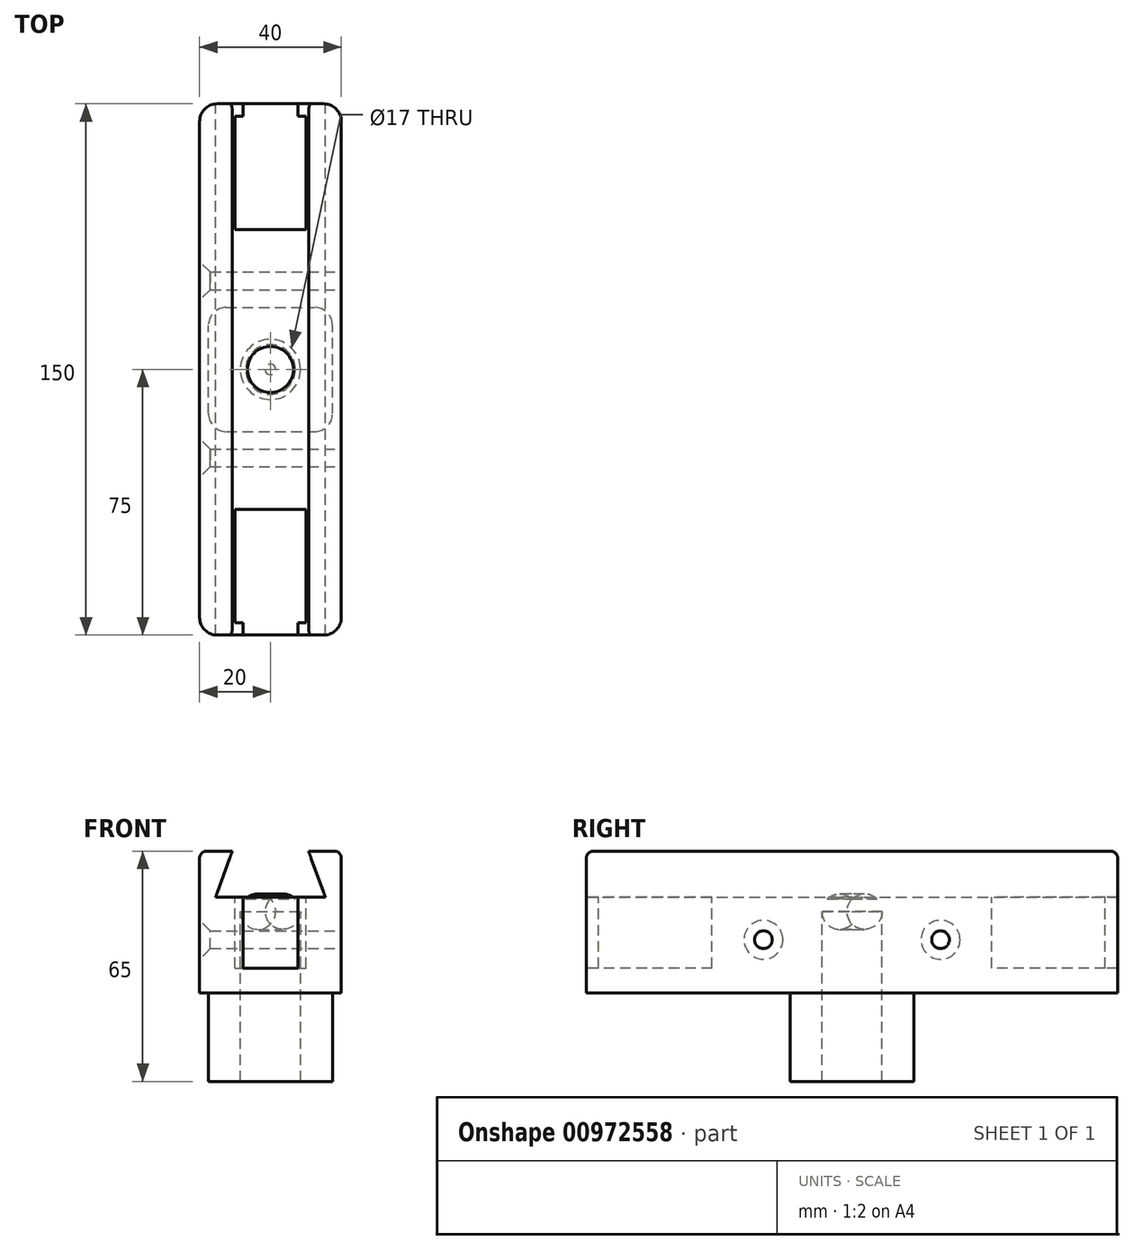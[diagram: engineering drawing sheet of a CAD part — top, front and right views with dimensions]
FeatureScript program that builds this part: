
annotation { "Feature Type Name" : "Feature", "Feature Type Description" : "" }
export const myFeature = defineFeature(function(context is Context, id is Id, definition is map)
    precondition{}
    {
        {
            var Q0;
            Q0=qCreatedBy(makeId("Front.planeOp"),FACE);
            var sketch = newSketch(context, id + "F0", { "sketchPlane" : qUnion([Q0])});
            skLineSegment(sketch, "E0.bottom", {"start": v(-20, 13.5) * mm, "end": v(20, 13.5) * mm});
            skLineSegment(sketch, "E0.top", {"start": v(-20, -13.5) * mm, "end": v(20, -13.5) * mm});
            skLineSegment(sketch, "E0.left", {"start": v(-20, 13.5) * mm, "end": v(-20, -13.5) * mm});
            skLineSegment(sketch, "E0.right", {"start": v(20, 13.5) * mm, "end": v(20, -13.5) * mm});
            skPoint(sketch, "E0.middle", {"position": v(0, 0) * mm});
            skSolve(sketch);
        }
        {
            var Q0;
            Q0=makeQuery(id+"F0.imprint","IMPRINT",FACE,{"disambiguationData":[TD([[makeQuery(id+"F0.imprint","IMPRINT",EDGE,{"derivedFrom":sQuery(id+"F0.wireOp",EDGE,"E0.bottom")}),-1.0]])]});
            extrude(context, id + "F1", {"entities" : qUnion([Q0]), "depth" : 150 * mm, "offsetDistance" : 25 * mm});
        }
        {
            var Q0;
            Q0=makeQuery(id+"F1.opExtrude","SWEPT_FACE",FACE,{"disambiguationData":[OSD([sQuery(id+"F0.wireOp",EDGE,"E0.bottom")])]});
            var sketch = newSketch(context, id + "F2", { "sketchPlane" : qUnion([Q0])});
            skLineSegment(sketch, "E1", {"start": v(1.02, -154.13) * mm, "end": v(0, 16.76) * mm, "construction": true});
            skLineSegment(sketch, "E2", {"start": v(-20, -75) * mm, "end": v(29.97, -74.7) * mm, "construction": true});
            skLineSegment(sketch, "E3", {"start": v(-20, -75) * mm, "end": v(-25.89, -75.04) * mm, "construction": true});
            skCircle(sketch, "E4", {"center": v(0.55, -74.88) * mm, "radius": 7.75 * mm});
            skLineSegment(sketch, "E5.bottom", {"start": v(-10, -3.5) * mm, "end": v(10, -3.5) * mm});
            skLineSegment(sketch, "E5.top", {"start": v(-10, -35.5) * mm, "end": v(10, -35.5) * mm});
            skLineSegment(sketch, "E5.left", {"start": v(-10, -3.5) * mm, "end": v(-10, -35.5) * mm});
            skLineSegment(sketch, "E5.right", {"start": v(10, -3.5) * mm, "end": v(10, -35.5) * mm});
            skLineSegment(sketch, "E6.bottom", {"start": v(-10, -114.5) * mm, "end": v(10, -114.5) * mm});
            skLineSegment(sketch, "E6.top", {"start": v(-10, -146.5) * mm, "end": v(10, -146.5) * mm});
            skLineSegment(sketch, "E6.left", {"start": v(-10, -114.5) * mm, "end": v(-10, -146.5) * mm});
            skLineSegment(sketch, "E6.right", {"start": v(10, -114.5) * mm, "end": v(10, -146.5) * mm});
            skLineSegment(sketch, "E7.bottom", {"start": v(-7.75, 0) * mm, "end": v(7.75, 0) * mm});
            skLineSegment(sketch, "E7.top", {"start": v(-7.75, -3.5) * mm, "end": v(7.75, -3.5) * mm});
            skLineSegment(sketch, "E7.left", {"start": v(-7.75, 0) * mm, "end": v(-7.75, -3.5) * mm});
            skLineSegment(sketch, "E7.right", {"start": v(7.75, 0) * mm, "end": v(7.75, -3.5) * mm});
            skLineSegment(sketch, "E8.bottom", {"start": v(-7.75, -146.5) * mm, "end": v(7.75, -146.5) * mm});
            skLineSegment(sketch, "E8.top", {"start": v(-7.75, -150) * mm, "end": v(7.75, -150) * mm});
            skLineSegment(sketch, "E8.left", {"start": v(-7.75, -146.5) * mm, "end": v(-7.75, -150) * mm});
            skLineSegment(sketch, "E8.right", {"start": v(7.75, -146.5) * mm, "end": v(7.75, -150) * mm});
            skSolve(sketch);
        }
        {
            var Q0;
            Q0=makeQuery(id+"F2.imprint","IMPRINT",FACE,{"disambiguationData":[TD([[makeQuery(id+"F2.imprint","IMPRINT",EDGE,{"derivedFrom":sQuery(id+"F2.wireOp",EDGE,"E7.bottom")}),-1.0]])]});
            var Q1;
            Q1=makeQuery(id+"F2.imprint","IMPRINT",FACE,{"disambiguationData":[TD([[makeQuery(id+"F2.imprint","IMPRINT",EDGE,{"derivedFrom":sQuery(id+"F2.wireOp",EDGE,"E5.top")}),1.0]])]});
            var Q2;
            Q2=makeQuery(id+"F2.imprint","IMPRINT",FACE,{"disambiguationData":[TD([[makeQuery(id+"F2.imprint","IMPRINT",EDGE,{"derivedFrom":sQuery(id+"F2.wireOp",EDGE,"E6.bottom")}),-1.0]])]});
            var Q3;
            Q3=makeQuery(id+"F2.imprint","IMPRINT",FACE,{"disambiguationData":[TD([[makeQuery(id+"F2.imprint","IMPRINT",EDGE,{"derivedFrom":sQuery(id+"F2.wireOp",EDGE,"E8.top")}),1.0]])]});
            extrude(context, id + "F3", {"entities" : qUnion([Q0, Q1, Q2, Q3]), "operationType" : NewBodyOperationType.REMOVE, "oppositeDirection" : true, "depth" : 20 * mm, "offsetDistance" : 25 * mm});
        }
        {
            var Q0;
            Q0=makeQuery(id+"F1.opExtrude","SWEPT_FACE",FACE,{"disambiguationData":[OSD([sQuery(id+"F0.wireOp",EDGE,"E0.top")])]});
            var sketch = newSketch(context, id + "F4", { "sketchPlane" : qUnion([Q0])});
            skLineSegment(sketch, "E9", {"start": v(0, 153.56) * mm, "end": v(0, -4.66) * mm, "construction": true});
            skLineSegment(sketch, "E10", {"start": v(-27.94, 75) * mm, "end": v(35.68, 75) * mm, "construction": true});
            skPoint(sketch, "E10.startSnap0", {"position": v(-20, 75) * mm});
            skCircle(sketch, "E11", {"center": v(0, 75) * mm, "radius": 8.5 * mm});
            skSolve(sketch);
        }
        {
            var Q0;
            Q0=makeQuery(id+"F4.imprint","IMPRINT",FACE,{"disambiguationData":[TD([[makeQuery(id+"F4.imprint","IMPRINT",EDGE,{"derivedFrom":sQuery(id+"F4.wireOp",EDGE,"E11")}),-1.0]])]});
            var sketch = newSketch(context, id + "F5", { "sketchPlane" : qUnion([Q0])});
            skLineSegment(sketch, "E12.bottom", {"start": v(-17.5, 92.5) * mm, "end": v(17.5, 92.5) * mm});
            skLineSegment(sketch, "E12.top", {"start": v(-17.5, 57.5) * mm, "end": v(17.5, 57.5) * mm});
            skLineSegment(sketch, "E12.left", {"start": v(-17.5, 92.5) * mm, "end": v(-17.5, 57.5) * mm});
            skLineSegment(sketch, "E12.right", {"start": v(17.5, 92.5) * mm, "end": v(17.5, 57.5) * mm});
            skPoint(sketch, "E12.middle", {"position": v(0, 75) * mm});
            skSolve(sketch);
        }
        {
            var Q0;
            Q0=makeQuery(id+"F5.imprint","IMPRINT",FACE,{"disambiguationData":[TD([[makeQuery(id+"F5.imprint","IMPRINT",EDGE,{"derivedFrom":sQuery(id+"F5.wireOp",EDGE,"E12.bottom")}),-1.0]])]});
            extrude(context, id + "F6", {"entities" : qUnion([Q0]), "operationType" : NewBodyOperationType.ADD, "depth" : 25 * mm, "offsetDistance" : 25 * mm});
        }
        {
            var Q0;
            Q0=makeQuery(id+"F4.imprint","IMPRINT",FACE,{"disambiguationData":[TD([[makeQuery(id+"F4.imprint","IMPRINT",EDGE,{"derivedFrom":sQuery(id+"F4.wireOp",EDGE,"E11")}),1.0]])]});
            extrude(context, id + "F7", {"entities" : qUnion([Q0]), "operationType" : NewBodyOperationType.REMOVE, "oppositeDirection" : true, "depth" : 25 * mm, "offsetDistance" : 25 * mm});
        }
        {
            var Q0;
            Q0=makeQuery(id+"F1.opExtrude","SWEPT_FACE",FACE,{"disambiguationData":[OSD([sQuery(id+"F0.wireOp",EDGE,"E0.bottom")])]});
            var sketch = newSketch(context, id + "F8", { "sketchPlane" : qUnion([Q0])});
            skLineSegment(sketch, "E13", {"start": v(0, 0) * mm, "end": v(0, -150.24) * mm, "construction": true});
            skLineSegment(sketch, "E14", {"start": v(-20, -75) * mm, "end": v(33, -75) * mm, "construction": true});
            skCircle(sketch, "E15", {"center": v(0, -75) * mm, "radius": 5.5 * mm});
            skSolve(sketch);
        }
        {
            var Q0;
            Q0=makeQuery(id+"F8.imprint","IMPRINT",FACE,{"disambiguationData":[TD([[makeQuery(id+"F8.imprint","IMPRINT",EDGE,{"derivedFrom":sQuery(id+"F8.wireOp",EDGE,"E15")}),1.0]])]});
            extrude(context, id + "F9", {"entities" : qUnion([Q0]), "operationType" : NewBodyOperationType.REMOVE, "endBound" : BoundingType.THROUGH_ALL, "oppositeDirection" : true, "depth" : 2 * mm, "offsetDistance" : 25 * mm});
        }
        {
            var Q0;
            Q0=makeQuery(id+"F9.boolean.opBoolean","INTERSECT",EDGE,{"derivedFrom":[makeQuery(id+"F7.boolean.opBoolean","COPY",FACE,{"derivedFrom":makeQuery(id+"F7.opExtrude","CAP_FACE",FACE,{"disambiguationData":[OSD([sQuery(id+"F4.wireOp",EDGE,"E11")])],"isStart":false})}),makeQuery(id+"F9.opExtrude","SWEPT_FACE",FACE,{"disambiguationData":[OSD([sQuery(id+"F8.wireOp",EDGE,"E15")])]})]});
            chamfer(context, id + "F10", {"entities" : qUnion([Q0]), "width" : 3 * mm, "tangentPropagation" : true});
        }
        {
            var Q0;
            {var subQ0=sQuery(id+"F4.wireOp",EDGE,"E11");Q0=makeQuery(id+"F10.opChamfer","BLEND_EDGE",EDGE,{"blendedFrom":[makeQuery(id+"F9.boolean.opBoolean","INTERSECT",EDGE,{"derivedFrom":[makeQuery(id+"F7.boolean.opBoolean","COPY",FACE,{"derivedFrom":makeQuery(id+"F7.opExtrude","CAP_FACE",FACE,{"disambiguationData":[OSD([subQ0])],"isStart":false})}),makeQuery(id+"F9.opExtrude","SWEPT_FACE",FACE,{"disambiguationData":[OSD([sQuery(id+"F8.wireOp",EDGE,"E15")])]})]}),makeQuery(id+"F7.boolean.opBoolean","MERGE",FACE,{"derivedFrom":[makeQuery(id+"F6.opExtrude","SWEPT_FACE",FACE,{"disambiguationData":[OSD([subQ0])]})],"fromTools":[makeQuery(id+"F7.opExtrude","SWEPT_FACE",FACE,{"disambiguationData":[OSD([subQ0])]})]})],"blendedInto":[makeQuery(id+"F7.boolean.opBoolean","MERGE",FACE,{"derivedFrom":[makeQuery(id+"F6.opExtrude","SWEPT_FACE",FACE,{"disambiguationData":[OSD([subQ0])]})],"fromTools":[makeQuery(id+"F7.opExtrude","SWEPT_FACE",FACE,{"disambiguationData":[OSD([subQ0])]})]})]});}
            fillet(context, id + "F11", {"entities" : qUnion([Q0]), "radius" : 5 * mm, "tangentPropagation" : true, "allowEdgeOverflow" : false});
        }
        {
            var Q0;
            Q0=qCreatedBy(makeId("Front.planeOp"),FACE);
            var sketch = newSketch(context, id + "F12", { "sketchPlane" : qUnion([Q0])});
            skLineSegment(sketch, "E16.bottom", {"start": v(-20, 13.5) * mm, "end": v(20, 13.5) * mm});
            skLineSegment(sketch, "E16.top", {"start": v(-20, 26.5) * mm, "end": v(20, 26.5) * mm});
            skLineSegment(sketch, "E16.left", {"start": v(-20, 13.5) * mm, "end": v(-20, 26.5) * mm});
            skLineSegment(sketch, "E16.right", {"start": v(20, 13.5) * mm, "end": v(20, 26.5) * mm});
            skLineSegment(sketch, "E17", {"start": v(-15.5, 13.5) * mm, "end": v(15.5, 13.5) * mm});
            skLineSegment(sketch, "E18", {"start": v(15.5, 13.5) * mm, "end": v(10.77, 26.5) * mm});
            skLineSegment(sketch, "E19", {"start": v(10.77, 26.5) * mm, "end": v(-10.77, 26.5) * mm});
            skLineSegment(sketch, "E20", {"start": v(-10.77, 26.5) * mm, "end": v(-15.5, 13.5) * mm});
            skLineSegment(sketch, "E21", {"start": v(-15.5, 13.5) * mm, "end": v(-15.5, 27.62) * mm, "construction": true});
            skLineSegment(sketch, "E22", {"start": v(15.5, 13.5) * mm, "end": v(15.5, 28) * mm, "construction": true});
            skSolve(sketch);
        }
        {
            var Q0;
            {var subQ0=sQuery(id+"F12.wireOp",EDGE,"E16.right");Q0=makeQuery(id+"F12.imprint","IMPRINT",FACE,{"disambiguationData":[TD([[makeQuery(id+"F12.imprint","IMPRINT",EDGE,{"derivedFrom":subQ0}),1.0]])]});}
            var Q1;
            {var subQ0=sQuery(id+"F12.wireOp",EDGE,"E16.left");Q1=makeQuery(id+"F12.imprint","IMPRINT",FACE,{"disambiguationData":[TD([[makeQuery(id+"F12.imprint","IMPRINT",EDGE,{"derivedFrom":subQ0}),-1.0]])]});}
            var Q2;
            Q2=makeQuery(id+"F1.opExtrude","CAP_FACE",FACE,{"disambiguationData":[OSD([sQuery(id+"F0.wireOp",EDGE,"E0.bottom"),sQuery(id+"F0.wireOp",EDGE,"E0.top"),sQuery(id+"F0.wireOp",EDGE,"E0.left"),sQuery(id+"F0.wireOp",EDGE,"E0.right")])],"isStart":false});
            extrude(context, id + "F13", {"entities" : qUnion([Q0, Q1]), "operationType" : NewBodyOperationType.ADD, "endBound" : BoundingType.UP_TO_SURFACE, "depth" : 25 * mm, "endBoundEntityFace" : qUnion([Q2]), "offsetDistance" : 25 * mm});
        }
        {
            var Q0;
            Q0=makeQuery(id+"F13.boolean.opBoolean","MERGE",EDGE,{"derivedFrom":[makeQuery(id+"F1.opExtrude","CAP_EDGE",EDGE,{"disambiguationData":[OSD([sQuery(id+"F0.wireOp",EDGE,"E0.left")])],"isStart":false}),makeQuery(id+"F13.opExtrude","CAP_EDGE",EDGE,{"disambiguationData":[OSD([sQuery(id+"F12.wireOp",EDGE,"E16.left")])],"isStart":false})]});
            var Q1;
            Q1=makeQuery(id+"F13.boolean.opBoolean","MERGE",EDGE,{"derivedFrom":[makeQuery(id+"F1.opExtrude","CAP_EDGE",EDGE,{"disambiguationData":[OSD([sQuery(id+"F0.wireOp",EDGE,"E0.right")])],"isStart":false}),makeQuery(id+"F13.opExtrude","CAP_EDGE",EDGE,{"disambiguationData":[OSD([sQuery(id+"F12.wireOp",EDGE,"E16.right")])],"isStart":false})]});
            var Q2;
            Q2=makeQuery(id+"F13.boolean.opBoolean","MERGE",EDGE,{"derivedFrom":[makeQuery(id+"F1.opExtrude","CAP_EDGE",EDGE,{"disambiguationData":[OSD([sQuery(id+"F0.wireOp",EDGE,"E0.right")])],"isStart":true}),makeQuery(id+"F13.opExtrude","CAP_EDGE",EDGE,{"disambiguationData":[OSD([sQuery(id+"F12.wireOp",EDGE,"E16.right")])],"isStart":true})]});
            var Q3;
            Q3=makeQuery(id+"F13.boolean.opBoolean","MERGE",EDGE,{"derivedFrom":[makeQuery(id+"F1.opExtrude","CAP_EDGE",EDGE,{"disambiguationData":[OSD([sQuery(id+"F0.wireOp",EDGE,"E0.left")])],"isStart":true}),makeQuery(id+"F13.opExtrude","CAP_EDGE",EDGE,{"disambiguationData":[OSD([sQuery(id+"F12.wireOp",EDGE,"E16.left")])],"isStart":true})]});
            var Q4;
            Q4=makeQuery(id+"F6.opExtrude","SWEPT_EDGE",EDGE,{"disambiguationData":[OSD([sQuery(id+"F5.wireOp",EDGE,"E12.top"),sQuery(id+"F5.wireOp",EDGE,"E12.right")])]});
            var Q5;
            Q5=makeQuery(id+"F6.opExtrude","SWEPT_EDGE",EDGE,{"disambiguationData":[OSD([sQuery(id+"F5.wireOp",EDGE,"E12.bottom"),sQuery(id+"F5.wireOp",EDGE,"E12.right")])]});
            var Q6;
            Q6=makeQuery(id+"F6.opExtrude","SWEPT_EDGE",EDGE,{"disambiguationData":[OSD([sQuery(id+"F5.wireOp",EDGE,"E12.top"),sQuery(id+"F5.wireOp",EDGE,"E12.left")])]});
            var Q7;
            Q7=makeQuery(id+"F6.opExtrude","SWEPT_EDGE",EDGE,{"disambiguationData":[OSD([sQuery(id+"F5.wireOp",EDGE,"E12.bottom"),sQuery(id+"F5.wireOp",EDGE,"E12.left")])]});
            fillet(context, id + "F14", {"entities" : qUnion([Q0, Q1, Q2, Q3, Q4, Q5, Q6, Q7]), "radius" : 5 * mm, "tangentPropagation" : true, "allowEdgeOverflow" : false});
        }
        {
            var Q0;
            {var subQ0=sQuery(id+"F12.wireOp",EDGE,"E16.top");Q0=makeQuery(id+"F13.opExtrude","CAP_EDGE",EDGE,{"disambiguationData":[OSD([subQ0]),TDD([makeQuery(id+"F12.imprint","IMPRINT",EDGE,{"disambiguationData":[TD([[makeQuery(id+"F12.imprint","INTERSECT",VERTEX,{"derivedFrom":[subQ0,sQuery(id+"F12.wireOp",EDGE,"E16.left")]}),-1.0]])],"derivedFrom":subQ0})])],"isStart":false});}
            var Q1;
            {var subQ0=sQuery(id+"F12.wireOp",EDGE,"E16.top");Q1=makeQuery(id+"F13.opExtrude","CAP_EDGE",EDGE,{"disambiguationData":[OSD([subQ0]),TDD([makeQuery(id+"F12.imprint","IMPRINT",EDGE,{"disambiguationData":[TD([[makeQuery(id+"F12.imprint","INTERSECT",VERTEX,{"derivedFrom":[subQ0,sQuery(id+"F12.wireOp",EDGE,"E16.right")]}),1.0]])],"derivedFrom":subQ0})])],"isStart":false});}
            fillet(context, id + "F15", {"entities" : qUnion([Q0, Q1]), "radius" : 2 * mm, "tangentPropagation" : true, "allowEdgeOverflow" : false});
        }
        {
            var Q0;
            Q0=qCreatedBy(makeId("Right.planeOp"),FACE);
            var sketch = newSketch(context, id + "F16", { "sketchPlane" : qUnion([Q0])});
            skCircle(sketch, "E23", {"center": v(-100, 1.5) * mm, "radius": 2.5 * mm});
            skCircle(sketch, "E24", {"center": v(-50, 1.5) * mm, "radius": 2.5 * mm});
            skSolve(sketch);
        }
        {
            var Q0;
            Q0=makeQuery(id+"F16.imprint","IMPRINT",FACE,{"disambiguationData":[TD([[makeQuery(id+"F16.imprint","IMPRINT",EDGE,{"derivedFrom":sQuery(id+"F16.wireOp",EDGE,"E23")}),1.0]])]});
            var Q1;
            Q1=makeQuery(id+"F16.imprint","IMPRINT",FACE,{"disambiguationData":[TD([[makeQuery(id+"F16.imprint","IMPRINT",EDGE,{"derivedFrom":sQuery(id+"F16.wireOp",EDGE,"E24")}),1.0]])]});
            extrude(context, id + "F17", {"entities" : qUnion([Q0, Q1]), "operationType" : NewBodyOperationType.REMOVE, "endBound" : BoundingType.THROUGH_ALL, "oppositeDirection" : true, "depth" : 25 * mm, "offsetDistance" : 25 * mm, "hasSecondDirection" : true, "secondDirectionOppositeDirection" : false, "secondDirectionDepth" : 25 * mm});
        }
        {
            var Q0;
            Q0=makeQuery(id+"F17.boolean.opBoolean","INTERSECT",EDGE,{"derivedFrom":[makeQuery(id+"F13.boolean.opBoolean","MERGE",FACE,{"derivedFrom":[makeQuery(id+"F1.opExtrude","SWEPT_FACE",FACE,{"disambiguationData":[OSD([sQuery(id+"F0.wireOp",EDGE,"E0.left")])]}),makeQuery(id+"F13.opExtrude","SWEPT_FACE",FACE,{"disambiguationData":[OSD([sQuery(id+"F12.wireOp",EDGE,"E16.left")])]})]}),makeQuery(id+"F17.opExtrude","SWEPT_FACE",FACE,{"disambiguationData":[OSD([sQuery(id+"F16.wireOp",EDGE,"E24")])]})]});
            var Q1;
            Q1=makeQuery(id+"F17.boolean.opBoolean","INTERSECT",EDGE,{"derivedFrom":[makeQuery(id+"F13.boolean.opBoolean","MERGE",FACE,{"derivedFrom":[makeQuery(id+"F1.opExtrude","SWEPT_FACE",FACE,{"disambiguationData":[OSD([sQuery(id+"F0.wireOp",EDGE,"E0.left")])]}),makeQuery(id+"F13.opExtrude","SWEPT_FACE",FACE,{"disambiguationData":[OSD([sQuery(id+"F12.wireOp",EDGE,"E16.left")])]})]}),makeQuery(id+"F17.opExtrude","SWEPT_FACE",FACE,{"disambiguationData":[OSD([sQuery(id+"F16.wireOp",EDGE,"E23")])]})]});
            chamfer(context, id + "F18", {"entities" : qUnion([Q0, Q1]), "width" : 3 * mm, "tangentPropagation" : true});
        }
    });
